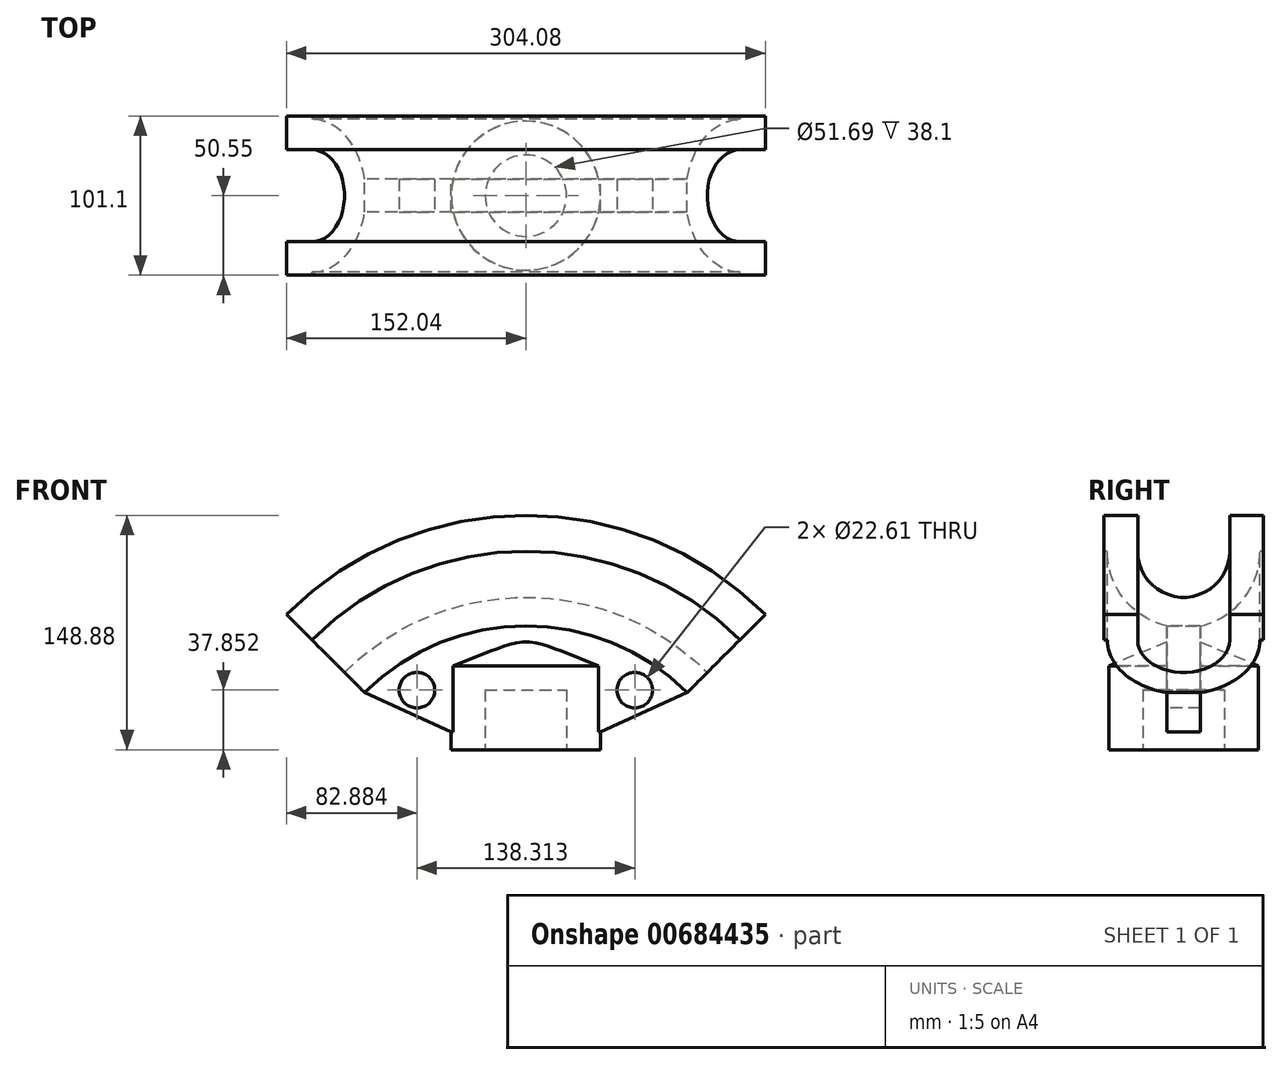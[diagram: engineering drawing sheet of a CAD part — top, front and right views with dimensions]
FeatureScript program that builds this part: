
annotation { "Feature Type Name" : "Feature", "Feature Type Description" : "" }
export const myFeature = defineFeature(function(context is Context, id is Id, definition is map)
    precondition{}
    {
        {
            var Q0;
            Q0=qCreatedBy(makeId("Front.planeOp"),FACE);
            var sketch = newSketch(context, id + "F0", { "sketchPlane" : qUnion([Q0])});
            skLineSegment(sketch, "E0", {"start": v(-47.37, 11.18) * mm, "end": v(47.37, 11.18) * mm});
            skPoint(sketch, "E1", {"position": v(0, -10.41) * mm});
            skLineSegment(sketch, "E2", {"start": v(47.37, 11.18) * mm, "end": v(102.38, 36.25) * mm});
            skLineSegment(sketch, "E3", {"start": v(-47.37, 11.18) * mm, "end": v(-102.38, 36.25) * mm});
            skPoint(sketch, "E4", {"position": v(0, -66.14) * mm});
            skArc(sketch, "E5", {"start": v(-102.38, 36.25) * mm, "mid": v(0, 78.65) * mm, "end": v(102.38, 36.25) * mm});
            skSolve(sketch);
        }
        {
            var Q0;
            Q0 = qSketchRegion(id + "F0", true);
            var Q1;
            Q1 = qSketchRegion(id + "F2", true);
            extrude(context, id + "F1", {"entities" : qUnion([Q0, Q1]), "endBound" : BoundingType.SYMMETRIC, "depth" : 21.08 * mm, "offsetDistance" : 25.4 * mm});
        }
        {
            var Q0;
            Q0=qCreatedBy(makeId("Right.planeOp"),FACE);
            var sketch = newSketch(context, id + "F2", { "sketchPlane" : qUnion([Q0])});
            skLineSegment(sketch, "E6", {"start": v(-10.54, 78.66) * mm, "end": v(10.54, 78.66) * mm});
            skArc(sketch, "E7", {"start": v(-48.51, 126.02) * mm, "mid": v(-37.85, 95.67) * mm, "end": v(-10.54, 78.66) * mm});
            skArc(sketch, "E8", {"start": v(-29.21, 126.02) * mm, "mid": v(0, 96.8) * mm, "end": v(29.21, 126.02) * mm});
            skArc(sketch, "E9.trimOffspring", {"start": v(10.54, 78.66) * mm, "mid": v(37.85, 95.67) * mm, "end": v(48.51, 126.02) * mm});
            skLineSegment(sketch, "E10", {"start": v(-29.21, 126.02) * mm, "end": v(-29.21, 148.88) * mm});
            skLineSegment(sketch, "E11", {"start": v(-29.21, 148.88) * mm, "end": v(-50.55, 148.88) * mm});
            skLineSegment(sketch, "E12", {"start": v(-50.55, 148.88) * mm, "end": v(-50.55, 126.02) * mm});
            skLineSegment(sketch, "E13", {"start": v(-50.55, 126.02) * mm, "end": v(-48.51, 126.02) * mm});
            skLineSegment(sketch, "E14.MirrorCS", {"start": v(29.21, 148.88) * mm, "end": v(50.55, 148.88) * mm});
            skLineSegment(sketch, "E15.MirrorCS", {"start": v(50.55, 148.88) * mm, "end": v(50.55, 126.02) * mm});
            skLineSegment(sketch, "E16.MirrorCS", {"start": v(29.21, 126.02) * mm, "end": v(29.21, 148.88) * mm});
            skLineSegment(sketch, "E17.MirrorCS", {"start": v(50.55, 126.02) * mm, "end": v(48.51, 126.02) * mm});
            skLineSegment(sketch, "E18", {"start": v(-84.92, -66.14) * mm, "end": v(98.98, -66.14) * mm, "construction": true});
            skPoint(sketch, "E19", {"position": v(0, 78.66) * mm});
            skSolve(sketch);
        }
        {
            var Q0;
            Q0=makeQuery(id+"F2.imprint","IMPRINT",FACE,{"disambiguationData":[TD([[makeQuery(id+"F2.imprint","IMPRINT",EDGE,{"derivedFrom":sQuery(id+"F2.wireOp",EDGE,"E6")}),1.0]])]});
            var Q1;
            Q1=sQuery(id+"F2.wireOp",EDGE,"E18");
            revolve(context, id + "F3", {"entities" : qUnion([Q0]), "axis" : qUnion([Q1]), "revolveType" : RevolveType.SYMMETRIC, "angle" : 90 * degree});
        }
        {
            var Q0;
            Q0=qCreatedBy(makeId("Right.planeOp"),FACE);
            var sketch = newSketch(context, id + "F4", { "sketchPlane" : qUnion([Q0])});
            skLineSegment(sketch, "E20", {"start": v(0, 0) * mm, "end": v(-47.37, 0) * mm});
            skLineSegment(sketch, "E21", {"start": v(-47.37, 0) * mm, "end": v(-47.37, 53.34) * mm});
            skLineSegment(sketch, "E22", {"start": v(-47.37, 53.34) * mm, "end": v(0, 72.9) * mm});
            skLineSegment(sketch, "E23", {"start": v(0, 72.9) * mm, "end": v(0, 0) * mm});
            skSolve(sketch);
        }
        {
            var Q0;
            Q0=makeQuery(id+"F4.imprint","IMPRINT",FACE,{"disambiguationData":[TD([[makeQuery(id+"F4.imprint","IMPRINT",EDGE,{"derivedFrom":sQuery(id+"F4.wireOp",EDGE,"E20")}),-1.0]])]});
            var Q1;
            Q1=sQuery(id+"F4.wireOp",EDGE,"E23");
            revolve(context, id + "F5", {"operationType" : NewBodyOperationType.ADD, "entities" : qUnion([Q0]), "axis" : qUnion([Q1]), "revolveType" : RevolveType.FULL});
        }
        {
            var Q0;
            Q0=makeQuery(id+"F1.opExtrude","CAP_FACE",FACE,{"disambiguationData":[OSD([sQuery(id+"F0.wireOp",EDGE,"E0"),sQuery(id+"F0.wireOp",EDGE,"E2"),sQuery(id+"F0.wireOp",EDGE,"E3"),sQuery(id+"F0.wireOp",EDGE,"E5")])],"isStart":false});
            var sketch = newSketch(context, id + "F6", { "sketchPlane" : qUnion([Q0])});
            skCircle(sketch, "E24", {"center": v(-69.16, 37.85) * mm, "radius": 11.3 * mm});
            skCircle(sketch, "E25.MirrorC", {"center": v(69.16, 37.85) * mm, "radius": 11.3 * mm});
            skSolve(sketch);
        }
        {
            var Q0;
            Q0 = qSketchRegion(id + "F6", true);
            extrude(context, id + "F7", {"entities" : qUnion([Q0]), "operationType" : NewBodyOperationType.REMOVE, "oppositeDirection" : true, "depth" : 25.4 * mm, "offsetDistance" : 25.4 * mm});
        }
        {
            var Q0;
            Q0=makeQuery(id+"F5.opRevolve","SWEPT_FACE",FACE,{"disambiguationData":[OSD([sQuery(id+"F4.wireOp",EDGE,"E20")])]});
            var sketch = newSketch(context, id + "F8", { "sketchPlane" : qUnion([Q0])});
            skCircle(sketch, "E26", {"center": v(0, 0) * mm, "radius": 25.84 * mm});
            skSolve(sketch);
        }
        {
            var Q0;
            Q0 = qSketchRegion(id + "F8", true);
            extrude(context, id + "F9", {"entities" : qUnion([Q0]), "operationType" : NewBodyOperationType.REMOVE, "oppositeDirection" : true, "depth" : 38.1 * mm, "offsetDistance" : 25.4 * mm});
        }
    });
